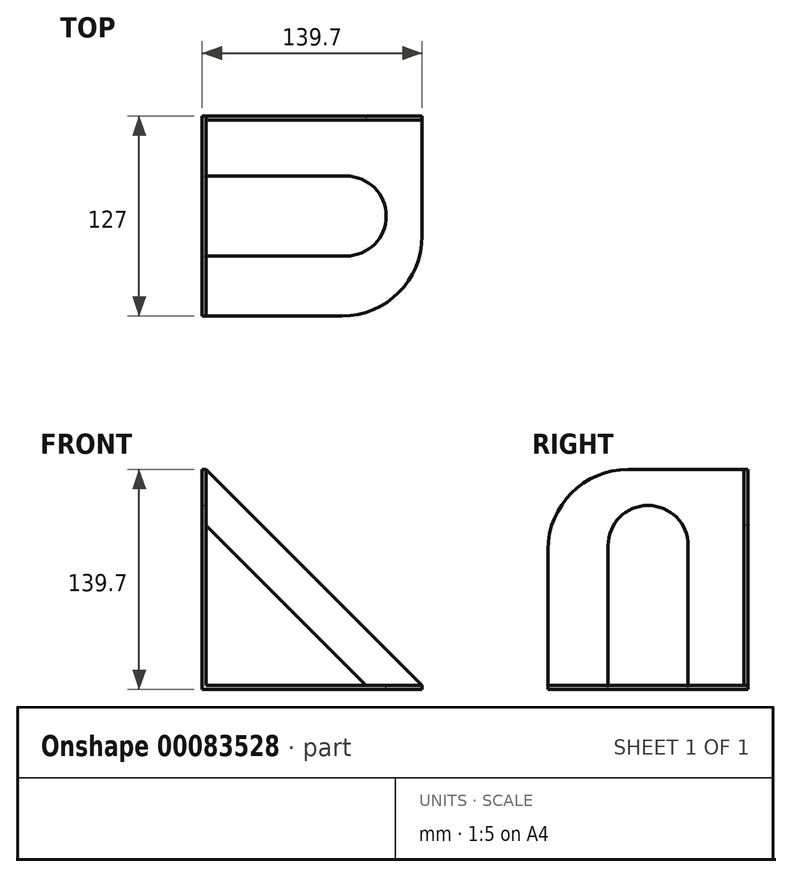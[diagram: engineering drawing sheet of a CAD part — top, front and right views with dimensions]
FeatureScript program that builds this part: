
annotation { "Feature Type Name" : "Feature", "Feature Type Description" : "" }
export const myFeature = defineFeature(function(context is Context, id is Id, definition is map)
    precondition{}
    {
        {
            var Q0;
            Q0=qCreatedBy(makeId("Top.planeOp"),FACE);
            var sketch = newSketch(context, id + "F0", { "sketchPlane" : qUnion([Q0])});
            skLineSegment(sketch, "E0.bottom", {"start": v(0, 0) * mm, "end": v(-139.7, 0) * mm});
            skLineSegment(sketch, "E0.top", {"start": v(0, -127) * mm, "end": v(-139.7, -127) * mm});
            skLineSegment(sketch, "E0.left", {"start": v(0, 0) * mm, "end": v(0, -127) * mm});
            skLineSegment(sketch, "E0.right", {"start": v(-139.7, 0) * mm, "end": v(-139.7, -127) * mm});
            skSolve(sketch);
        }
        {
            var Q0;
            Q0 = qSketchRegion(id + "F0", true);
            extrude(context, id + "F1", {"entities" : qUnion([Q0]), "depth" : 139.7 * mm});
        }
        {
            var Q0;
            Q0=makeQuery(id+"F1.opExtrude","SWEPT_FACE",FACE,{"disambiguationData":[OSD([sQuery(id+"F0.wireOp",EDGE,"E0.top")])]});
            var sketch = newSketch(context, id + "F2", { "sketchPlane" : qUnion([Q0])});
            skLineSegment(sketch, "E1.bottom", {"start": v(0, 139.7) * mm, "end": v(-137.16, 139.7) * mm});
            skLineSegment(sketch, "E1.top", {"start": v(0, 2.54) * mm, "end": v(-137.16, 2.54) * mm});
            skLineSegment(sketch, "E1.left", {"start": v(0, 139.7) * mm, "end": v(0, 2.54) * mm});
            skLineSegment(sketch, "E1.right", {"start": v(-137.16, 139.7) * mm, "end": v(-137.16, 2.54) * mm});
            skSolve(sketch);
        }
        {
            var Q0;
            Q0 = qSketchRegion(id + "F2", true);
            extrude(context, id + "F3", {"entities" : qUnion([Q0]), "operationType" : NewBodyOperationType.REMOVE, "oppositeDirection" : true, "depth" : 124.46 * mm});
        }
        {
            var Q0;
            Q0=makeQuery(id+"F3.boolean.opBoolean","COPY",FACE,{"derivedFrom":makeQuery(id+"F3.opExtrude","CAP_FACE",FACE,{"disambiguationData":[OSD([sQuery(id+"F2.wireOp",EDGE,"E1.bottom"),sQuery(id+"F2.wireOp",EDGE,"E1.top"),sQuery(id+"F2.wireOp",EDGE,"E1.left"),sQuery(id+"F2.wireOp",EDGE,"E1.right")])],"isStart":false})});
            var sketch = newSketch(context, id + "F4", { "sketchPlane" : qUnion([Q0])});
            skLineSegment(sketch, "E2", {"start": v(-137.16, 139.7) * mm, "end": v(0, 2.54) * mm});
            skLineSegment(sketch, "E3", {"start": v(0, 2.54) * mm, "end": v(55.8, 142.75) * mm});
            skLineSegment(sketch, "E4", {"start": v(55.8, 142.75) * mm, "end": v(-6.92, 178.29) * mm});
            skLineSegment(sketch, "E5", {"start": v(-6.92, 178.29) * mm, "end": v(-137.16, 139.7) * mm});
            skSolve(sketch);
        }
        {
            var Q0;
            Q0 = qSketchRegion(id + "F4", true);
            extrude(context, id + "F5", {"entities" : qUnion([Q0]), "operationType" : NewBodyOperationType.REMOVE, "oppositeDirection" : true, "depth" : 25.4 * mm});
        }
        {
            var Q0;
            Q0=makeQuery(id+"F3.boolean.opBoolean","COPY",FACE,{"derivedFrom":makeQuery(id+"F3.opExtrude","CAP_FACE",FACE,{"disambiguationData":[OSD([sQuery(id+"F2.wireOp",EDGE,"E1.bottom"),sQuery(id+"F2.wireOp",EDGE,"E1.top"),sQuery(id+"F2.wireOp",EDGE,"E1.left"),sQuery(id+"F2.wireOp",EDGE,"E1.right")])],"isStart":false})});
            var sketch = newSketch(context, id + "F6", { "sketchPlane" : qUnion([Q0])});
            skLineSegment(sketch, "E6", {"start": v(-137.16, 2.54) * mm, "end": v(-35.56, 2.54) * mm});
            skLineSegment(sketch, "E7", {"start": v(-35.56, 2.54) * mm, "end": v(-137.16, 104.14) * mm});
            skLineSegment(sketch, "E8", {"start": v(-137.16, 104.14) * mm, "end": v(-137.16, 2.54) * mm});
            skSolve(sketch);
        }
        {
            var Q0;
            Q0 = qSketchRegion(id + "F6", true);
            extrude(context, id + "F7", {"entities" : qUnion([Q0]), "operationType" : NewBodyOperationType.REMOVE, "oppositeDirection" : true, "depth" : 25.4 * mm});
        }
        {
            var Q0;
            Q0=makeQuery(id+"F7.boolean.opBoolean","MERGE",FACE,{"derivedFrom":[makeQuery(id+"F3.boolean.opBoolean","COPY",FACE,{"derivedFrom":makeQuery(id+"F3.opExtrude","SWEPT_FACE",FACE,{"disambiguationData":[OSD([sQuery(id+"F2.wireOp",EDGE,"E1.top")])]})}),makeQuery(id+"F7.opExtrude","SWEPT_FACE",FACE,{"disambiguationData":[OSD([sQuery(id+"F6.wireOp",EDGE,"E6")])]})]});
            var sketch = newSketch(context, id + "F8", { "sketchPlane" : qUnion([Q0])});
            skLineSegment(sketch, "E9", {"start": v(-137.16, -88.9) * mm, "end": v(-48.26, -88.9) * mm});
            skLineSegment(sketch, "E10", {"start": v(-48.26, -38.1) * mm, "end": v(-137.16, -38.1) * mm});
            skLineSegment(sketch, "E11", {"start": v(-137.16, -38.1) * mm, "end": v(-137.16, -88.9) * mm});
            skArc(sketch, "E12", {"start": v(-48.26, -88.9) * mm, "mid": v(-22.86, -63.5) * mm, "end": v(-48.26, -38.1) * mm});
            skSolve(sketch);
        }
        {
            var Q0;
            Q0 = qSketchRegion(id + "F8", true);
            extrude(context, id + "F9", {"entities" : qUnion([Q0]), "operationType" : NewBodyOperationType.REMOVE, "oppositeDirection" : true, "depth" : 25.4 * mm});
        }
        {
            var Q0;
            Q0=makeQuery(id+"F9.boolean.opBoolean","MERGE",FACE,{"derivedFrom":[makeQuery(id+"F7.boolean.opBoolean","MERGE",FACE,{"derivedFrom":[makeQuery(id+"F3.boolean.opBoolean","COPY",FACE,{"derivedFrom":makeQuery(id+"F3.opExtrude","SWEPT_FACE",FACE,{"disambiguationData":[OSD([sQuery(id+"F2.wireOp",EDGE,"E1.right")])]})}),makeQuery(id+"F7.opExtrude","SWEPT_FACE",FACE,{"disambiguationData":[OSD([sQuery(id+"F6.wireOp",EDGE,"E8")])]})]}),makeQuery(id+"F9.opExtrude","SWEPT_FACE",FACE,{"disambiguationData":[OSD([sQuery(id+"F8.wireOp",EDGE,"E11")])]})]});
            var sketch = newSketch(context, id + "F10", { "sketchPlane" : qUnion([Q0])});
            skLineSegment(sketch, "E13", {"start": v(-38.1, 2.54) * mm, "end": v(-38.1, 91.44) * mm});
            skLineSegment(sketch, "E14", {"start": v(-88.9, 2.54) * mm, "end": v(-88.9, 91.44) * mm});
            skArc(sketch, "E15", {"start": v(-38.1, 91.44) * mm, "mid": v(-63.5, 116.84) * mm, "end": v(-88.9, 91.44) * mm});
            skSolve(sketch);
        }
        {
            var Q0;
            Q0 = qSketchRegion(id + "F10", true);
            var Q1;
            Q1=makeQuery(id+"F10.imprint","IMPRINT",FACE,{"disambiguationData":[TD([[makeQuery(id+"F10.imprint","IMPRINT",EDGE,{"derivedFrom":sQuery(id+"F10.wireOp",EDGE,"E13")}),1.0]])]});
            extrude(context, id + "F11", {"entities" : qUnion([Q0, Q1]), "operationType" : NewBodyOperationType.REMOVE, "oppositeDirection" : true, "depth" : 25.4 * mm});
        }
        {
            var Q0;
            Q0=makeQuery(id+"F1.opExtrude","SWEPT_EDGE",EDGE,{"disambiguationData":[OSD([sQuery(id+"F0.wireOp",EDGE,"E0.top"),sQuery(id+"F0.wireOp",EDGE,"E0.left")])]});
            var Q1;
            Q1=makeQuery(id+"F1.opExtrude","CAP_EDGE",EDGE,{"disambiguationData":[OSD([sQuery(id+"F0.wireOp",EDGE,"E0.top")])],"isStart":false});
            fillet(context, id + "F12", {"entities" : qUnion([Q0, Q1]), "radius" : 50.8 * mm, "tangentPropagation" : true, "allowEdgeOverflow" : false});
        }
    });
